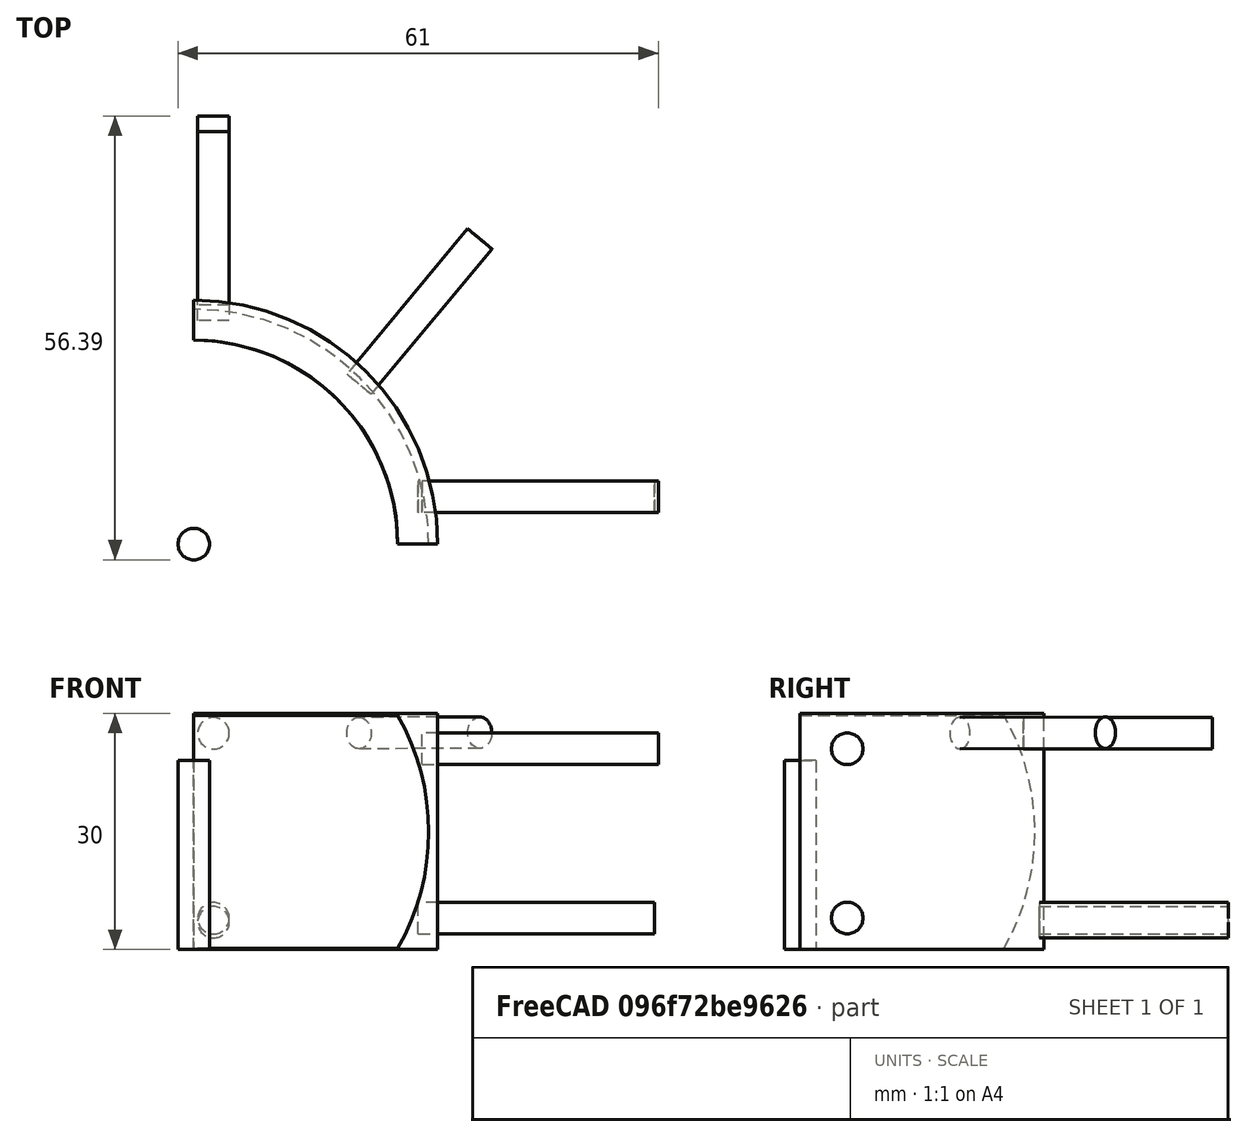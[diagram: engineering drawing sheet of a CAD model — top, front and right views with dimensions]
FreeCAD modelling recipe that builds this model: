
FCSTD DOCUMENT  (FreeCAD 1.1R43908 (Git))
Label: door_handle2
License: All rights reserved
LicenseURL: https://en.wikipedia.org/wiki/All_rights_reserved
objects: Part::Cylinder×7, Sketcher::SketchObject×3, App::Point×2, Mesh::Feature×1, PartDesign::FeatureBase×1, PartDesign::Pad×1, PartDesign::Groove×1, PartDesign::Body×1, App::Part×1
note: 22 computed .brp shape members not serialized (recipe doc carries the construction recipe); baked Part::Feature solids carry a one-line shape summary decoded from their .brp

FEATURE [Sketcher::SketchObject] Sketch
  ArcFitTolerance = 1e-06
  AttachmentSupport = -> [Origin]
  ExternalTypes = [0]
  FullyConstrained = true
  MakeInternals = false
  MapMode = 5
  sketch-geometry (6):
    g0: ArcOfCircle CenterX=0 CenterY=0 CenterZ=0 NormalX=0 NormalY=0 NormalZ=1 AngleXU=0 Radius=25.9 StartAngle=3.26795e-07 EndAngle=1.5708
    g1: LineSegment StartX=1.6e-15 StartY=25.9 StartZ=0 EndX=1.6e-15 EndY=30.9 EndZ=0
    g2: LineSegment StartX=25.9 StartY=8.46399e-06 StartZ=0 EndX=30.9 EndY=0 EndZ=0
    g3: ArcOfCircle CenterX=0 CenterY=0 CenterZ=0 NormalX=0 NormalY=0 NormalZ=1 AngleXU=0 Radius=30.98 StartAngle=0 EndAngle=1.5708
    g4: LineSegment StartX=30.9 StartY=0 StartZ=0 EndX=30.98 EndY=0 EndZ=0
    g5: LineSegment StartX=1.6e-15 StartY=30.9 StartZ=0 EndX=1.9e-15 EndY=30.98 EndZ=0
  constraints (18):
    c: Radius(g0) = 25.9
    c: Angle(g0) = 1.5708
    c: Coincident(g0,g-1)
    c: Distance(g1) = 5
    c: Coincident(g1,g0)
    c: PointOnObject(g1,g-2)
    c: Vertical(g1)
    c: Distance(g2) = 5
    c: Coincident(g2,g0)
    c: PointOnObject(g2,g-1)
    c: Radius(g3) = 30.98
    c: Coincident(g3,g0)
    c: PointOnObject(g3,g-2)
    c: PointOnObject(g3,g-1)
    c: Coincident(g4,g2)
    c: Coincident(g4,g3)
    c: Coincident(g5,g1)
    c: Coincident(g5,g3)
FEATURE [App::Point] Origin001
  Role = Origin
FEATURE [Sketcher::SketchObject] Sketch001
  ArcFitTolerance = 1e-06
  AttachmentSupport = -> [Origin]
  ExternalTypes = [0]
  FullyConstrained = false
  MakeInternals = false
  MapMode = 5
  Placement = pos=(0,0,0) rot=(1,0,0;1.5708rad)
  sketch-geometry (2):
    g0: ArcOfCircle CenterX=0 CenterY=14.9449 CenterZ=0 NormalX=0 NormalY=0 NormalZ=1 AngleXU=0 Radius=29.841 StartAngle=5.75864 EndAngle=6.80773
    g1: LineSegment StartX=25.8289 StartY=29.8898 StartZ=0 EndX=25.8289 EndY=-1.07e-14 EndZ=0
  constraints (5):
    c: PointOnObject(g0,g-2)
    c: PointOnObject(g0,g-1)
    c: Coincident(g1,g0)
    c: Coincident(g1,g0)
    c: Parallel(g1,g-2)
FEATURE [App::Point] Origin003
  Role = Origin
FEATURE [Mesh::Feature] doornob_arc
  Placement = pos=(191,148,0) rot=(0,0,1;3.14159rad)
FEATURE [Part::Cylinder] Cylinder006
  Angle = 360
  AttacherType = Attacher::AttachEngine3D
  FirstAngle = 0
  Height = 24
  Placement = pos=(2.5,52.39,27.47) rot=(1,0,0;1.5708rad)
  Radius = 2
  SecondAngle = 0
FEATURE [Part::Cylinder] Cylinder007
  Angle = 360
  AttacherType = Attacher::AttachEngine3D
  FirstAngle = 0
  Height = 24
  Placement = pos=(2.5,54.39,3.97) rot=(1,0,0;1.5708rad)
  Radius = 2
  SecondAngle = 0
FEATURE [Part::Cylinder] Cylinder
  Angle = 360
  AttacherType = Attacher::AttachEngine3D
  FirstAngle = 0
  Height = 30
  Placement = pos=(29,6,25.5) rot=(0,1,0;1.5708rad)
  Radius = 2
  SecondAngle = 0
FEATURE [Part::Cylinder] Cylinder008
  Angle = 360
  AttacherType = Attacher::AttachEngine3D
  FirstAngle = 0
  Height = 24
  Placement = pos=(2.5,54.39,3.47) rot=(1,0,0;1.5708rad)
  Radius = 2
  SecondAngle = 0
FEATURE [Part::Cylinder] Cylinder009
  Angle = 360
  AttacherType = Attacher::AttachEngine3D
  FirstAngle = 0
  Height = 24
  Placement = pos=(20.9857,20.3292,27.4999) rot=(0.39,-0.83,-0.39;4.5328rad)
  Radius = 2
  SecondAngle = 0
FEATURE [Part::Cylinder] Cylinder010
  Angle = 360
  AttacherType = Attacher::AttachEngine3D
  FirstAngle = 0
  Height = 30
  Placement = pos=(28.5,6,4) rot=(0,1,0;1.5708rad)
  Radius = 2
  SecondAngle = 0
FEATURE [Part::Cylinder] Cylinder011
  Angle = 360
  AttacherType = Attacher::AttachEngine3D
  FirstAngle = 0
  Height = 24
  Placement = pos=(21.03,20.35,4) rot=(0.39,-0.83,-0.39;4.5328rad)
  Radius = 2
  SecondAngle = 0
FEATURE [PartDesign::FeatureBase] BaseFeature
  BaseFeature = -> Cylinder011
  Suppressed = false
FEATURE [PartDesign::Pad] Pad
  BaseFeature = -> BaseFeature
  Direction = (0,0,1)
  Length = 30
  Length2 = 10
  Profile = -> Sketch
  ReferenceAxis = -> Sketch [N_Axis]
  Refine = true
  SideType = 0
  Suppressed = false
  Type = 0
  Type2 = 0
FEATURE [Sketcher::SketchObject] Sketch002
  ArcFitTolerance = 1e-06
  AttachmentSupport = -> [Pad]
  ExternalTypes = [0]
  FullyConstrained = true
  MakeInternals = false
  MapMode = 5
  Placement = pos=(1.9e-15,0,0) rot=(0.57735,-0.57735,-0.57735;2.0944rad)
FEATURE [PartDesign::Groove] Groove
  Angle = 360
  Angle2 = 0
  Axis = (0,2e-16,1)
  Base = (0,0,0)
  BaseFeature = -> Pad
  Profile = -> Sketch001
  ReferenceAxis = -> Sketch001 [V_Axis]
  Refine = true
  Suppressed = false
  Type = 0
FEATURE [PartDesign::Body] Body
  AllowCompound = true
  BaseFeature = -> Cylinder011
  Group = -> [BaseFeature,Sketch,Pad,Sketch001,Groove]
  Origin = -> Origin
  Tip = -> Groove
FEATURE [App::Part] Part
  Group = -> [Body,Cylinder010,Cylinder006,doornob_arc,Cylinder007,Cylinder,Cylinder011,Cylinder008,Cylinder009]
  Origin = -> Origin002
